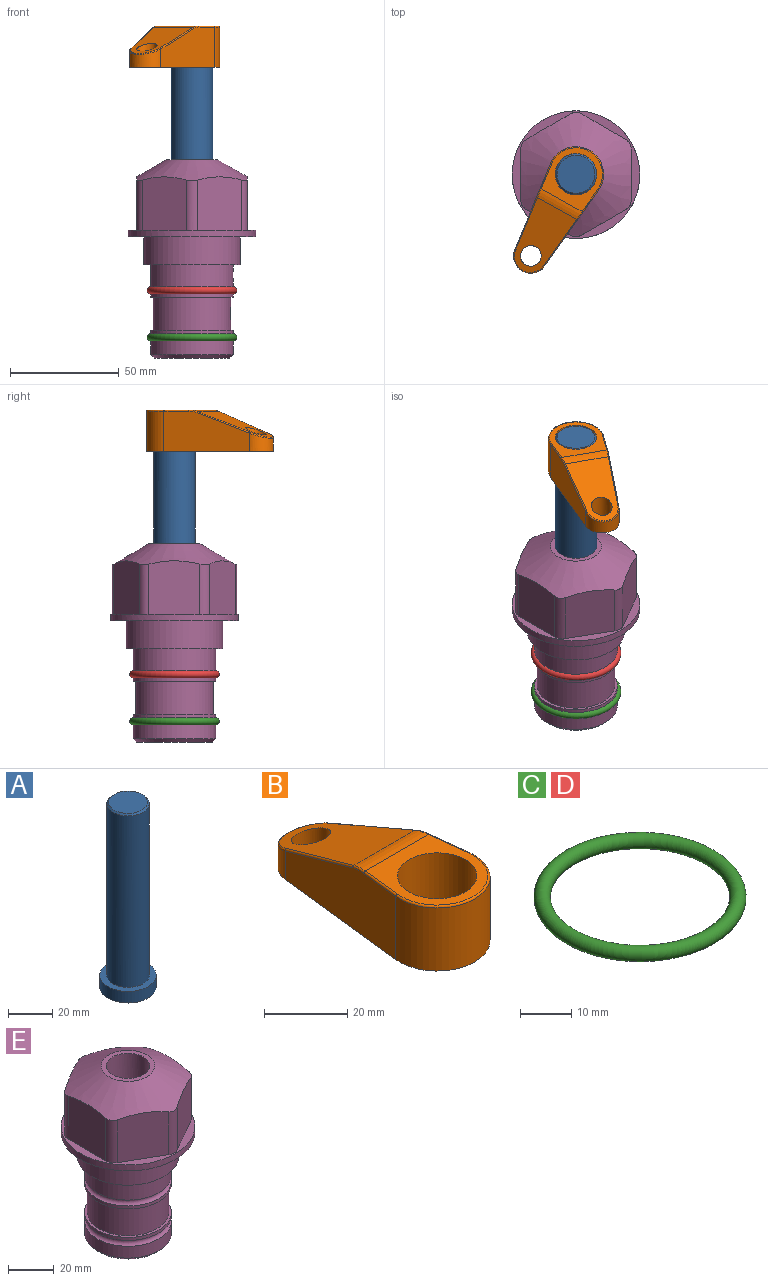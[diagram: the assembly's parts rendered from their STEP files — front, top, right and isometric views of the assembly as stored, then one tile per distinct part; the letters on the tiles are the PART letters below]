
ASSEMBLY  parts=5 mates=3
PART A: 6 faces, bbox 25.4x25.4x101.6 mm
  f0: plane 17.46x17.46mm, normal (0,0,1), area 239.5mm2, adj f5
  f1: plane 25.4x25.4mm, normal (0,0,-1), area 506.7mm2, adj f2
  f2: cylinder r=12.7mm len=25.4mm, axis (0,0,1), area 506.7mm2, adj f1,f3
  f3: plane 25.4x25.4mm, normal (0,0,1), area 221.7mm2, adj f2,f4
  f4: cylinder r=9.53mm len=94.46mm, axis (0,0,1), area 5653mm2, adj f3,f5
  f5: cone r=8.73mm half-angle=45deg, axis (0,0,-1), area 64.4mm2, adj f0,f4
PART B: 44 faces, bbox 27.5x64.5x19.1 mm
  f0: plane 2.3x0.95mm, normal (0,0,-1), area 1mm2, adj f25,f30,f34
  f1: plane 63.5x25.4mm, normal (0,0,-1), area 561.7mm2, adj f2,f3,f4,f5,f6,f7,f19,f20
  f2: cylinder r=12.7mm len=25.4mm, axis (0,0,-1), area 792.2mm2, adj f1,f3,f5,f13
  f3: plane 42.33x18.54mm, normal (0.99,0.11,0), area 647mm2, adj f1,f2,f4,f11,f12,f14
  f4: cylinder r=7.94mm len=15.78mm, axis (0,0,-1), area 158.6mm2, adj f1,f3,f5,f16
  f5: plane 42.33x18.54mm, normal (-0.99,0.11,0), area 647mm2, adj f1,f2,f4,f15,f17,f18
  f6: cylinder r=9.53mm len=19.05mm, axis (0,0,-1), area 1140.1mm2, adj f1,f8
  f7: cylinder r=4.76mm len=10.98mm, axis (0,0,-1), area 276.1mm2, adj f1,f9
  f8: plane 25.83x24.38mm, normal (0,0,1), area 262.2mm2, adj f6,f10,f11,f13,f15
  f9: plane 32.49x20.55mm, normal (0,0.34,0.94), area 489.9mm2, adj f7,f10,f14,f16,f18
  f10: cylinder r=12.7mm len=21.49mm, axis (-1,0,0), area 93.2mm2, adj f8,f9,f12,f17
  f11: cylinder r=0.51mm len=12.34mm, axis (0.11,-0.99,0), area 9.9mm2, adj f3,f8,f12,f13
  f12: bspline ~7.62x1.64mm, area 3.5mm2, adj f3,f10,f11,f14
  f13: torus R=12.19mm, axis (0,0,1), area 33.6mm2, adj f2,f8,f11,f15
  f14: cylinder r=0.51mm len=26.01mm, axis (0.1,-0.93,0.34), area 21.6mm2, adj f3,f9,f12,f16
  f15: cylinder r=0.51mm len=12.34mm, axis (0.11,0.99,0), area 9.9mm2, adj f5,f8,f13,f17
  f16: bspline ~15.78x7.05mm, area 15.7mm2, adj f4,f9,f14,f18
  f17: bspline ~7.62x1.64mm, area 3.5mm2, adj f5,f10,f15,f18
  f18: cylinder r=0.51mm len=26.01mm, axis (0.1,0.93,-0.34), area 21.6mm2, adj f5,f9,f16,f17
  f19: plane 21.6x14.29mm, normal (-0.99,-0.11,0), area 242.6mm2, adj f1,f26,f28,f34,f36,f38
  f20: plane 21.6x14.29mm, normal (0.99,-0.11,0), area 242.6mm2, adj f1,f27,f29,f37,f39,f41
  f21: cylinder r=12.7mm len=14.29mm, axis (0,0,-1), area 173.2mm2, adj f1,f26,f27,f30,f31,f33
  f22: cylinder r=7.94mm len=7.63mm, axis (0,0,-1), area 53.8mm2, adj f1,f28,f29,f42
  f23: plane 2.3x0.95mm, normal (0,0,-1), area 1mm2, adj f25,f33,f37
  f24: plane 17.94x12.32mm, normal (0,-0.34,-0.94), area 191.2mm2, adj f25,f38,f41,f42
  f25: cylinder r=9.53mm len=12.93mm, axis (-1,0,0), area 37.5mm2, adj f0,f23,f24,f31,f36,f39
  f26: cylinder r=1.59mm len=14.29mm, axis (0,0,-1), area 49mm2, adj f1,f19,f21,f32
  f27: cylinder r=1.59mm len=14.29mm, axis (0,0,-1), area 49mm2, adj f1,f20,f21,f35
  f28: cylinder r=1.59mm len=7.28mm, axis (0,0,-1), area 22.1mm2, adj f1,f19,f22,f40
  f29: cylinder r=1.59mm len=7.28mm, axis (0,0,-1), area 22.1mm2, adj f1,f20,f22,f43
  f30: torus R=14.29mm, axis (0,0,1), area 5.8mm2, adj f0,f21,f31,f32
  f31: bspline ~11.06x2.73mm, area 20.8mm2, adj f21,f25,f30,f33
  f32: sphere r=1.59mm, area 5.4mm2, adj f26,f30,f34
  f33: torus R=14.29mm, axis (0,0,1), area 5.8mm2, adj f21,f23,f31,f35
  f34: cylinder r=1.59mm len=1.68mm, axis (-0.11,0.99,0), area 2.4mm2, adj f0,f19,f32,f36
  f35: sphere r=1.59mm, area 5.4mm2, adj f27,f33,f37
  f36: bspline ~5.82x2.33mm, area 7.7mm2, adj f19,f25,f34,f38
  f37: cylinder r=1.59mm len=1.68mm, axis (0.11,0.99,0), area 2.4mm2, adj f20,f23,f35,f39
  f38: cylinder r=1.59mm len=18.33mm, axis (0.1,-0.93,0.34), area 46.7mm2, adj f19,f24,f36,f40
  f39: bspline ~5.82x2.33mm, area 7.7mm2, adj f20,f25,f37,f41
  f40: sphere r=1.59mm, area 3.6mm2, adj f28,f38,f42
  f41: cylinder r=1.59mm len=18.33mm, axis (0.1,0.93,-0.34), area 46.7mm2, adj f20,f24,f39,f43
  f42: bspline ~8.31x1.84mm, area 15.3mm2, adj f22,f24,f40,f43
  f43: sphere r=1.59mm, area 3.6mm2, adj f29,f41,f42
PART C: 1 faces, bbox 44.7x44.7x3.2 mm
  f0: torus R=19.05mm, axis (0,0,1), area 1193.9mm2
PART D: same geometry as C
PART E: 36 faces, bbox 58.7x58.7x91.2 mm
  f0: cylinder r=17.78mm len=35.56mm, axis (0,0,1), area 1670.8mm2, adj f23,f24,f31
  f1: cylinder r=19.05mm len=38.1mm, axis (0,0,1), area 1191.9mm2, adj f26,f27,f30
  f2: plane 58.66x58.66mm, normal (0,0,-1), area 1150.6mm2, adj f3,f28
  f3: cylinder r=29.33mm len=58.66mm, axis (0,0,-1), area 585.1mm2, adj f2,f4
  f4: plane 58.66x58.66mm, normal (0,0,1), area 475.9mm2, adj f3,f5,f6,f7,f8,f9,f10,f11
  f5: plane 24.5x20.32mm, normal (-0.5,0.87,0), area 562.8mm2, adj f4,f15,f16,f17
  f6: plane 24.5x20.32mm, normal (0.5,0.87,0), area 562.8mm2, adj f4,f14,f15,f17
  f7: plane 24.5x23.48mm, normal (1,0,0), area 562.8mm2, adj f4,f13,f14,f17
  f8: plane 24.5x20.32mm, normal (0.5,-0.87,0), area 562.8mm2, adj f4,f12,f13,f17
  f9: plane 24.5x20.32mm, normal (-0.5,-0.87,0), area 562.8mm2, adj f4,f11,f12,f17
  f10: plane 24.5x23.48mm, normal (-1,0,0), area 562.8mm2, adj f4,f11,f16,f17
  f11: cylinder r=5.08mm len=23.01mm, axis (0,0,-1), area 121.2mm2, adj f4,f9,f10,f17
  f12: cylinder r=5.08mm len=23.01mm, axis (0,0,-1), area 121.2mm2, adj f4,f8,f9,f17
  f13: cylinder r=5.08mm len=23.01mm, axis (0,0,-1), area 121.2mm2, adj f4,f7,f8,f17
  f14: cylinder r=5.08mm len=23.01mm, axis (0,0,-1), area 121.2mm2, adj f4,f6,f7,f17
  f15: cylinder r=5.08mm len=23.01mm, axis (0,0,-1), area 121.2mm2, adj f4,f5,f6,f17
  f16: cylinder r=5.08mm len=23.01mm, axis (0,0,-1), area 121.2mm2, adj f4,f5,f10,f17
  f17: cone r=11.73mm half-angle=60deg, axis (0,0,-1), area 2071.8mm2, adj f5,f6,f7,f8,f9,f10,f11,f12
  f18: plane 23.46x23.46mm, normal (0,0,1), area 147.4mm2, adj f17,f35
  f19: plane 34.93x34.93mm, normal (0,0,-1), area 958mm2, adj f29
  f20: cylinder r=19.05mm len=38.1mm, axis (0,0,1), area 760.1mm2, adj f21,f29
  f21: torus R=19.05mm, axis (0,0,1), area 565.3mm2, adj f20,f22
  f22: cylinder r=19.05mm len=38.1mm, axis (0,0,1), area 190mm2, adj f21,f23
  f23: plane 38.1x38.1mm, normal (0,0,1), area 146.9mm2, adj f0,f22
  f24: plane 38.1x38.1mm, normal (0,0,-1), area 146.9mm2, adj f0,f25
  f25: cylinder r=19.05mm len=38.1mm, axis (0,0,1), area 190mm2, adj f24,f26
  f26: torus R=19.05mm, axis (0,0,1), area 565.3mm2, adj f1,f25
  f27: plane 44.45x44.45mm, normal (0,0,-1), area 411.7mm2, adj f1,f28
  f28: cylinder r=22.23mm len=44.45mm, axis (0,0,1), area 1773.5mm2, adj f2,f27
  f29: cone r=19.05mm half-angle=45deg, axis (0,0,1), area 257.5mm2, adj f19,f20
  f30: cylinder r=3.17mm len=6.75mm, axis (-1,0,0), area 128mm2, adj f1,f33
  f31: cylinder r=3.17mm len=6.35mm, axis (-1,0,0), area 102.5mm2, adj f0,f33
  f32: plane 25.4x25.4mm, normal (0,0,1), area 506.7mm2, adj f33
  f33: cylinder r=12.7mm len=66.42mm, axis (0,0,-1), area 5236.2mm2, adj f30,f31,f32,f34
  f34: cone r=9.53mm half-angle=30deg, axis (0,0,-1), area 443.4mm2, adj f33,f35
  f35: cylinder r=9.53mm len=19.05mm, axis (0,0,-1), area 849mm2, adj f18,f34
PLACE A rot(axis=(0,0,-1),119deg) t=(0,0,23.33)mm
PLACE B rot(axis=(0,0,1),151deg) t=(0,0,77.94)mm
PLACE C t=(0,0,-21.59)mm
PLACE D at identity
PLACE E at identity fixed
MATE fastened C.f0 <-> E.f0  axis (0,0,1) through (0,0,-46.1)mm
MATE cylindrical A.f2 <-> E.f0  axis (0,0,1) through (0,0,48.97)mm
MATE fastened B.f2 <-> A.f2  axis (0,0,1) through (0,0,96.99)mm
